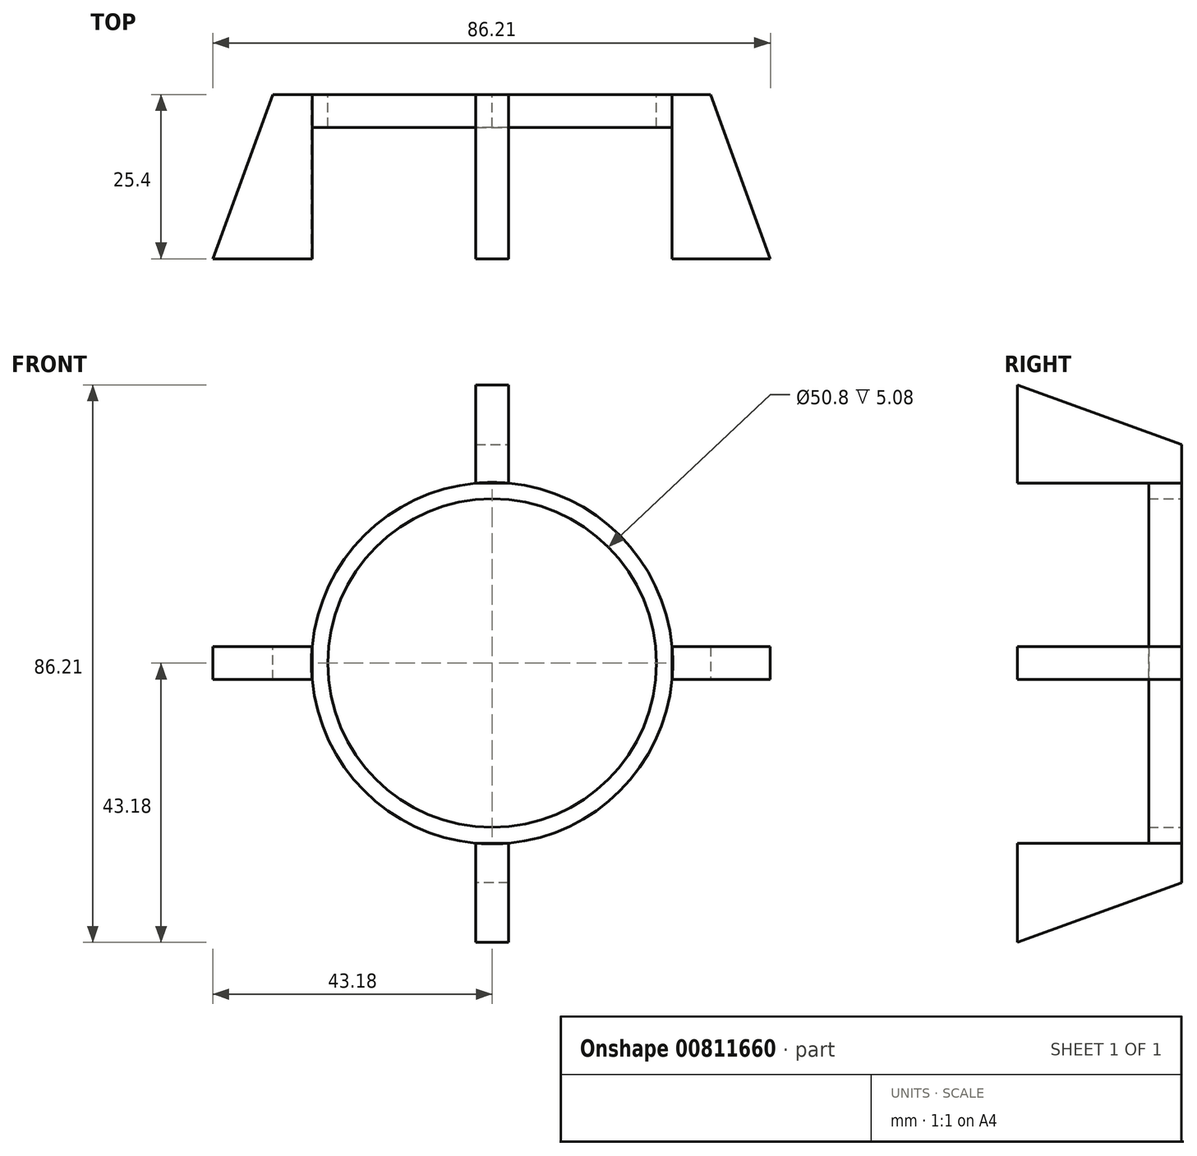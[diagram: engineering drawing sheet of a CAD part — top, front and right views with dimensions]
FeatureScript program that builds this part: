
annotation { "Feature Type Name" : "Feature", "Feature Type Description" : "" }
export const myFeature = defineFeature(function(context is Context, id is Id, definition is map)
    precondition{}
    {
        {
            var Q0;
            Q0=qCreatedBy(makeId("Front.planeOp"),FACE);
            var sketch = newSketch(context, id + "F0", { "sketchPlane" : qUnion([Q0])});
            skCircle(sketch, "E0", {"center": v(0, 0) * mm, "radius": 25.4 * mm});
            skCircle(sketch, "E1", {"center": v(0, 0) * mm, "radius": 27.94 * mm});
            skLineSegment(sketch, "E2", {"start": v(0, 0) * mm, "end": v(0, -43.18) * mm});
            skLineSegment(sketch, "E3", {"start": v(0, 0) * mm, "end": v(43.18, 0) * mm});
            skLineSegment(sketch, "E4", {"start": v(0, 0) * mm, "end": v(0, 43.18) * mm});
            skLineSegment(sketch, "E5", {"start": v(0, 0) * mm, "end": v(-43.18, 0) * mm});
            skLineSegment(sketch, "E6.bottom", {"start": v(0, -43.18) * mm, "end": v(2.54, -43.18) * mm});
            skLineSegment(sketch, "E6.top", {"start": v(0, -27.82) * mm, "end": v(2.54, -27.82) * mm});
            skLineSegment(sketch, "E6.left", {"start": v(0, -43.18) * mm, "end": v(0, -27.82) * mm});
            skLineSegment(sketch, "E6.right", {"start": v(2.54, -43.18) * mm, "end": v(2.54, -27.82) * mm});
            skLineSegment(sketch, "E7.bottom", {"start": v(0, -43.18) * mm, "end": v(-2.54, -43.18) * mm});
            skLineSegment(sketch, "E7.top", {"start": v(0, -27.82) * mm, "end": v(-2.54, -27.82) * mm});
            skLineSegment(sketch, "E7.right", {"start": v(-2.54, -43.18) * mm, "end": v(-2.54, -27.82) * mm});
            skLineSegment(sketch, "E8.bottom", {"start": v(43.18, 0) * mm, "end": v(27.82, 0) * mm});
            skLineSegment(sketch, "E8.top", {"start": v(43.18, -2.54) * mm, "end": v(27.82, -2.54) * mm});
            skLineSegment(sketch, "E8.left", {"start": v(43.18, 0) * mm, "end": v(43.18, -2.54) * mm});
            skLineSegment(sketch, "E8.right", {"start": v(27.82, 0) * mm, "end": v(27.82, -2.54) * mm});
            skLineSegment(sketch, "E9.top", {"start": v(43.18, 2.54) * mm, "end": v(27.82, 2.54) * mm});
            skLineSegment(sketch, "E9.left", {"start": v(43.18, 0) * mm, "end": v(43.18, 2.54) * mm});
            skLineSegment(sketch, "E9.right", {"start": v(27.82, 0) * mm, "end": v(27.82, 2.54) * mm});
            skLineSegment(sketch, "E10.bottom", {"start": v(0, 43.18) * mm, "end": v(2.53, 43.18) * mm});
            skLineSegment(sketch, "E10.top", {"start": v(0, 27.82) * mm, "end": v(2.53, 27.82) * mm});
            skLineSegment(sketch, "E10.left", {"start": v(0, 43.18) * mm, "end": v(0, 27.82) * mm});
            skLineSegment(sketch, "E10.right", {"start": v(2.53, 43.18) * mm, "end": v(2.53, 27.82) * mm});
            skLineSegment(sketch, "E11.bottom", {"start": v(0, 43.18) * mm, "end": v(-2.54, 43.18) * mm});
            skLineSegment(sketch, "E11.top", {"start": v(0, 27.82) * mm, "end": v(-2.54, 27.82) * mm});
            skLineSegment(sketch, "E11.right", {"start": v(-2.54, 43.18) * mm, "end": v(-2.54, 27.82) * mm});
            skLineSegment(sketch, "E12.bottom", {"start": v(-43.18, 0) * mm, "end": v(-27.82, 0) * mm});
            skLineSegment(sketch, "E12.top", {"start": v(-43.18, 2.54) * mm, "end": v(-27.82, 2.54) * mm});
            skLineSegment(sketch, "E12.left", {"start": v(-43.18, 0) * mm, "end": v(-43.18, 2.54) * mm});
            skLineSegment(sketch, "E12.right", {"start": v(-27.82, 0) * mm, "end": v(-27.82, 2.54) * mm});
            skLineSegment(sketch, "E13.top", {"start": v(-43.18, -2.54) * mm, "end": v(-27.82, -2.54) * mm});
            skLineSegment(sketch, "E13.left", {"start": v(-43.18, 0) * mm, "end": v(-43.18, -2.54) * mm});
            skLineSegment(sketch, "E13.right", {"start": v(-27.82, 0) * mm, "end": v(-27.82, -2.54) * mm});
            skSolve(sketch);
        }
        {
            var Q0;
            {var subQ4=sQuery(id+"F0.wireOp",EDGE,"E7.top");Q0=makeQuery(id+"F0.imprint","IMPRINT",FACE,{"disambiguationData":[TD([[makeQuery(id+"F0.imprint","IMPRINT",EDGE,{"derivedFrom":subQ4}),-1.0]])]});}
            var Q1;
            {var subQ0=sQuery(id+"F0.wireOp",EDGE,"E6.top");Q1=makeQuery(id+"F0.imprint","IMPRINT",FACE,{"disambiguationData":[TD([[makeQuery(id+"F0.imprint","IMPRINT",EDGE,{"derivedFrom":subQ0}),1.0]])]});}
            var Q2;
            {var subQ5=sQuery(id+"F0.wireOp",EDGE,"E9.right");Q2=makeQuery(id+"F0.imprint","IMPRINT",FACE,{"disambiguationData":[TD([[makeQuery(id+"F0.imprint","IMPRINT",EDGE,{"derivedFrom":subQ5}),1.0]])]});}
            var Q3;
            {var subQ6=sQuery(id+"F0.wireOp",EDGE,"E11.top");Q3=makeQuery(id+"F0.imprint","IMPRINT",FACE,{"disambiguationData":[TD([[makeQuery(id+"F0.imprint","IMPRINT",EDGE,{"derivedFrom":subQ6}),1.0]])]});}
            extrude(context, id + "F1", {"entities" : qUnion([Q0, Q1, Q2, Q3]), "depth" : 5.08 * mm, "offsetDistance" : 25.4 * mm});
        }
        {
            var Q0;
            {var subQ0=sQuery(id+"F0.wireOp",EDGE,"E13.top");Q0=makeQuery(id+"F0.imprint","IMPRINT",FACE,{"disambiguationData":[TD([[makeQuery(id+"F0.imprint","IMPRINT",EDGE,{"derivedFrom":subQ0}),1.0]])]});}
            var Q1;
            {var subQ0=sQuery(id+"F0.wireOp",EDGE,"E12.top");Q1=makeQuery(id+"F0.imprint","IMPRINT",FACE,{"disambiguationData":[TD([[makeQuery(id+"F0.imprint","IMPRINT",EDGE,{"derivedFrom":subQ0}),-1.0]])]});}
            var Q2;
            {var subQ4=sQuery(id+"F0.wireOp",EDGE,"E10.bottom");Q2=makeQuery(id+"F0.imprint","IMPRINT",FACE,{"disambiguationData":[TD([[makeQuery(id+"F0.imprint","IMPRINT",EDGE,{"derivedFrom":subQ4}),-1.0]])]});}
            var Q3;
            {var subQ4=sQuery(id+"F0.wireOp",EDGE,"E11.bottom");Q3=makeQuery(id+"F0.imprint","IMPRINT",FACE,{"disambiguationData":[TD([[makeQuery(id+"F0.imprint","IMPRINT",EDGE,{"derivedFrom":subQ4}),1.0]])]});}
            var Q4;
            {var subQ0=sQuery(id+"F0.wireOp",EDGE,"E8.top");Q4=makeQuery(id+"F0.imprint","IMPRINT",FACE,{"disambiguationData":[TD([[makeQuery(id+"F0.imprint","IMPRINT",EDGE,{"derivedFrom":subQ0}),-1.0]])]});}
            var Q5;
            {var subQ0=sQuery(id+"F0.wireOp",EDGE,"E9.top");Q5=makeQuery(id+"F0.imprint","IMPRINT",FACE,{"disambiguationData":[TD([[makeQuery(id+"F0.imprint","IMPRINT",EDGE,{"derivedFrom":subQ0}),1.0]])]});}
            var Q6;
            {var subQ4=sQuery(id+"F0.wireOp",EDGE,"E6.bottom");Q6=makeQuery(id+"F0.imprint","IMPRINT",FACE,{"disambiguationData":[TD([[makeQuery(id+"F0.imprint","IMPRINT",EDGE,{"derivedFrom":subQ4}),1.0]])]});}
            var Q7;
            {var subQ4=sQuery(id+"F0.wireOp",EDGE,"E7.bottom");Q7=makeQuery(id+"F0.imprint","IMPRINT",FACE,{"disambiguationData":[TD([[makeQuery(id+"F0.imprint","IMPRINT",EDGE,{"derivedFrom":subQ4}),-1.0]])]});}
            extrude(context, id + "F2", {"entities" : qUnion([Q0, Q1, Q2, Q3, Q4, Q5, Q6, Q7]), "depth" : 25.4 * mm, "offsetDistance" : 25.4 * mm});
        }
        {
            var Q0;
            Q0=makeQuery(id+"F2.opExtrude","CAP_EDGE",EDGE,{"disambiguationData":[OSD([sQuery(id+"F0.wireOp",EDGE,"E12.left"),sQuery(id+"F0.wireOp",EDGE,"E13.left")])],"isStart":true});
            chamfer(context, id + "F3", {"entities" : qUnion([Q0]), "chamferType" : ChamferType.OFFSET_ANGLE, "width" : 25.4 * mm, "oppositeDirection" : false, "angle" : 20 * degree, "tangentPropagation" : true});
        }
        {
            var Q0;
            Q0=makeQuery(id+"F2.opExtrude","CAP_EDGE",EDGE,{"disambiguationData":[OSD([sQuery(id+"F0.wireOp",EDGE,"E10.bottom"),sQuery(id+"F0.wireOp",EDGE,"E11.bottom")])],"isStart":true});
            chamfer(context, id + "F4", {"entities" : qUnion([Q0]), "chamferType" : ChamferType.OFFSET_ANGLE, "width" : 9.4 * mm, "oppositeDirection" : false, "angle" : 70 * degree, "tangentPropagation" : true});
        }
        {
            var Q0;
            Q0=makeQuery(id+"F2.opExtrude","CAP_EDGE",EDGE,{"disambiguationData":[OSD([sQuery(id+"F0.wireOp",EDGE,"E8.left"),sQuery(id+"F0.wireOp",EDGE,"E9.left")])],"isStart":true});
            chamfer(context, id + "F5", {"entities" : qUnion([Q0]), "chamferType" : ChamferType.OFFSET_ANGLE, "width" : 9.4 * mm, "oppositeDirection" : false, "angle" : 70 * degree, "tangentPropagation" : true});
        }
        {
            var Q0;
            Q0=makeQuery(id+"F2.opExtrude","CAP_EDGE",EDGE,{"disambiguationData":[OSD([sQuery(id+"F0.wireOp",EDGE,"E6.bottom"),sQuery(id+"F0.wireOp",EDGE,"E7.bottom")])],"isStart":true});
            chamfer(context, id + "F6", {"entities" : qUnion([Q0]), "chamferType" : ChamferType.OFFSET_ANGLE, "width" : 25.4 * mm, "oppositeDirection" : false, "angle" : 20 * degree, "tangentPropagation" : true});
        }
    });
